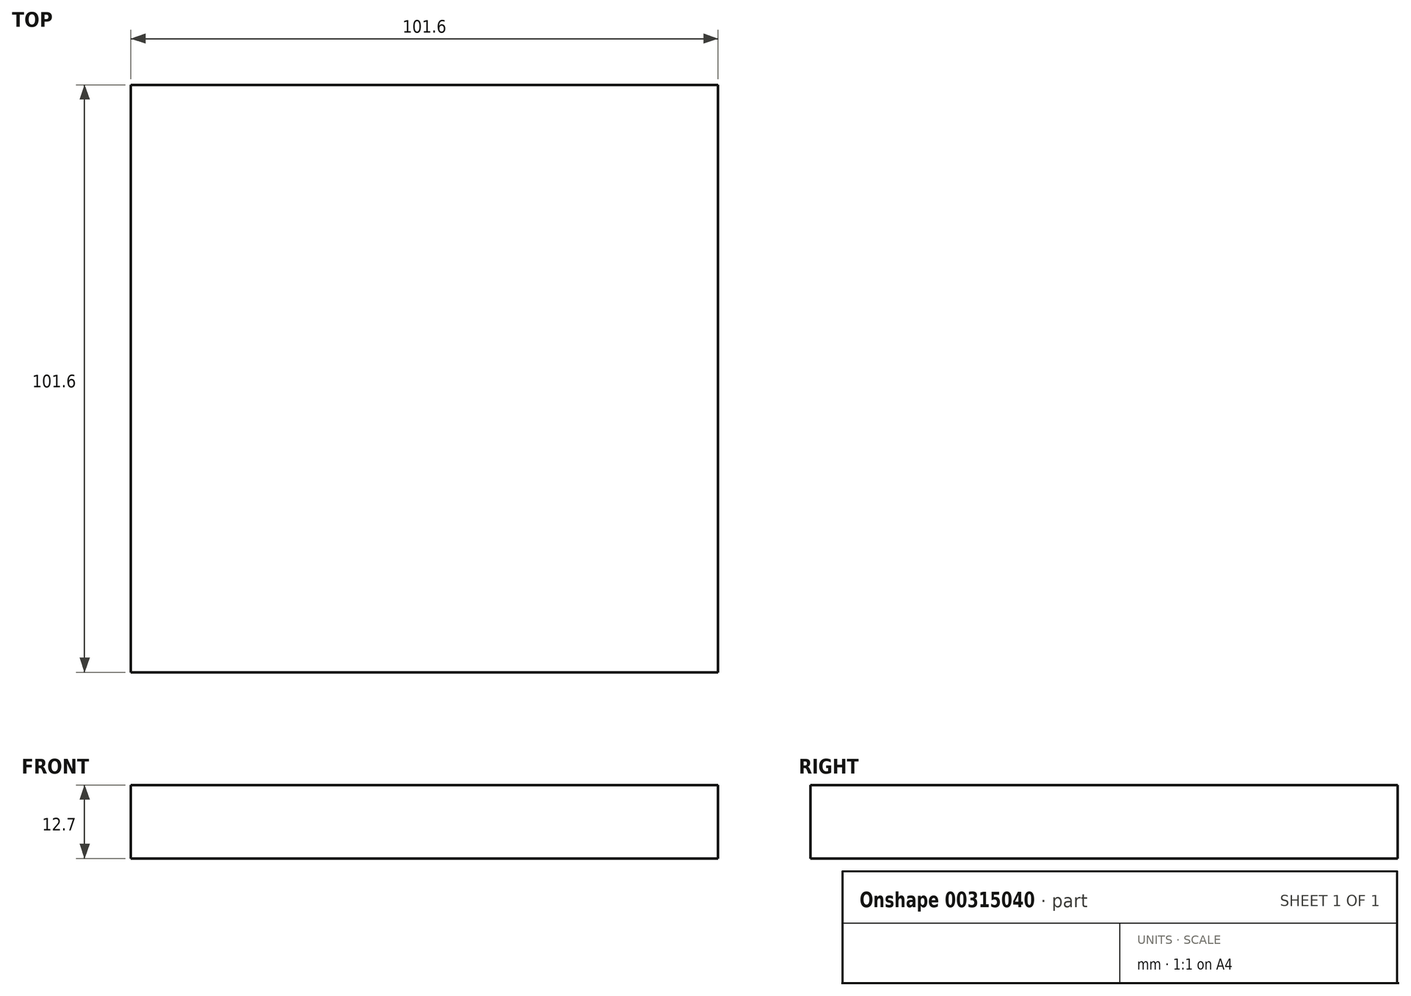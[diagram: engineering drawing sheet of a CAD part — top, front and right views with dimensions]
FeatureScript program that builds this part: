
annotation { "Feature Type Name" : "Feature", "Feature Type Description" : "" }
export const myFeature = defineFeature(function(context is Context, id is Id, definition is map)
    precondition{}
    {
        {
            var Q0;
            Q0=qCreatedBy(makeId("Front.planeOp"),FACE);
            var sketch = newSketch(context, id + "F0", { "sketchPlane" : qUnion([Q0])});
            skLineSegment(sketch, "E0", {"start": v(0, -12.7) * mm, "end": v(0, 0) * mm, "construction": true});
            skLineSegment(sketch, "E1", {"start": v(0, -12.7) * mm, "end": v(-50.8, -12.7) * mm});
            skLineSegment(sketch, "E2", {"start": v(-50.8, -12.7) * mm, "end": v(50.8, -12.7) * mm});
            skLineSegment(sketch, "E3", {"start": v(-50.8, -12.7) * mm, "end": v(-50.8, 0) * mm});
            skLineSegment(sketch, "E4", {"start": v(-50.8, 0) * mm, "end": v(50.8, 0) * mm});
            skLineSegment(sketch, "E5", {"start": v(50.8, 0) * mm, "end": v(50.8, -12.7) * mm});
            skSolve(sketch);
        }
        {
            var Q0;
            Q0=qSketchRegion(id+"F0",true);
            extrude(context, id + "F1", {"entities" : qUnion([Q0]), "endBound" : BoundingType.SYMMETRIC, "depth" : 101.6 * mm});
        }
    });
